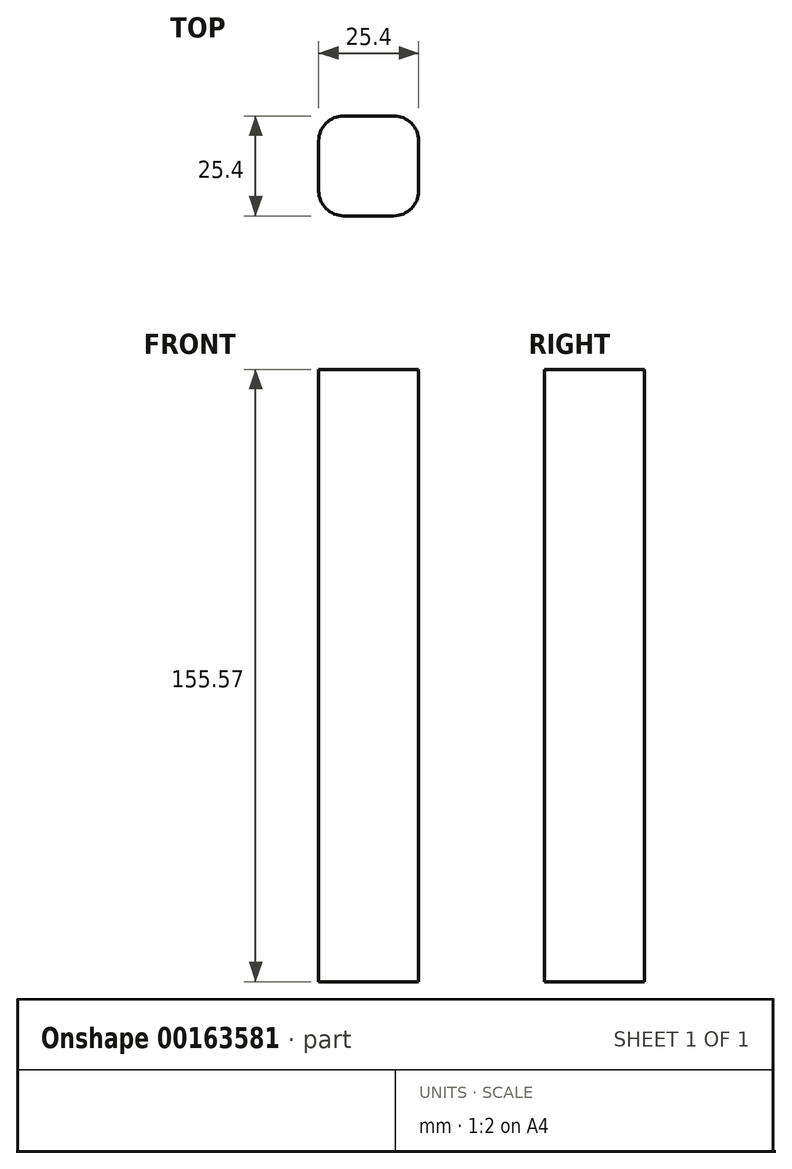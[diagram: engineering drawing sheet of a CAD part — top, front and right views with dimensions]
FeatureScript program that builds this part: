
annotation { "Feature Type Name" : "Feature", "Feature Type Description" : "" }
export const myFeature = defineFeature(function(context is Context, id is Id, definition is map)
    precondition{}
    {
        {
            var Q0;
            Q0=qCreatedBy(makeId("Top.planeOp"),FACE);
            var sketch = newSketch(context, id + "F0", { "sketchPlane" : qUnion([Q0])});
            skLineSegment(sketch, "E0.bottom", {"start": v(6.35, 12.7) * mm, "end": v(-6.35, 12.7) * mm});
            skLineSegment(sketch, "E0.top", {"start": v(6.35, -12.7) * mm, "end": v(-6.35, -12.7) * mm});
            skLineSegment(sketch, "E0.left", {"start": v(12.7, 6.35) * mm, "end": v(12.7, -6.35) * mm});
            skLineSegment(sketch, "E0.right", {"start": v(-12.7, 6.35) * mm, "end": v(-12.7, -6.35) * mm});
            skPoint(sketch, "E0.middle", {"position": v(0, 0) * mm});
            skPoint(sketch, "E1.visualSharp", {"position": v(-12.7, 12.7) * mm});
            skArc(sketch, "E1.filletArc", {"start": v(-6.35, 12.7) * mm, "mid": v(-10.84, 10.84) * mm, "end": v(-12.7, 6.35) * mm});
            skPoint(sketch, "E2.visualSharp", {"position": v(-12.7, -12.7) * mm});
            skArc(sketch, "E2.filletArc", {"start": v(-12.7, -6.35) * mm, "mid": v(-10.84, -10.84) * mm, "end": v(-6.35, -12.7) * mm});
            skPoint(sketch, "E3.visualSharp", {"position": v(12.7, -12.7) * mm});
            skArc(sketch, "E3.filletArc", {"start": v(6.35, -12.7) * mm, "mid": v(10.84, -10.84) * mm, "end": v(12.7, -6.35) * mm});
            skPoint(sketch, "E4.visualSharp", {"position": v(12.7, 12.7) * mm});
            skArc(sketch, "E4.filletArc", {"start": v(12.7, 6.35) * mm, "mid": v(10.84, 10.84) * mm, "end": v(6.35, 12.7) * mm});
            skSolve(sketch);
        }
        {
            var Q0;
            Q0=qSketchRegion(id+"F0",true);
            extrude(context, id + "F1", {"entities" : qUnion([Q0]), "depth" : 155.57 * mm, "offsetDistance" : 25.4 * mm});
        }
    });
